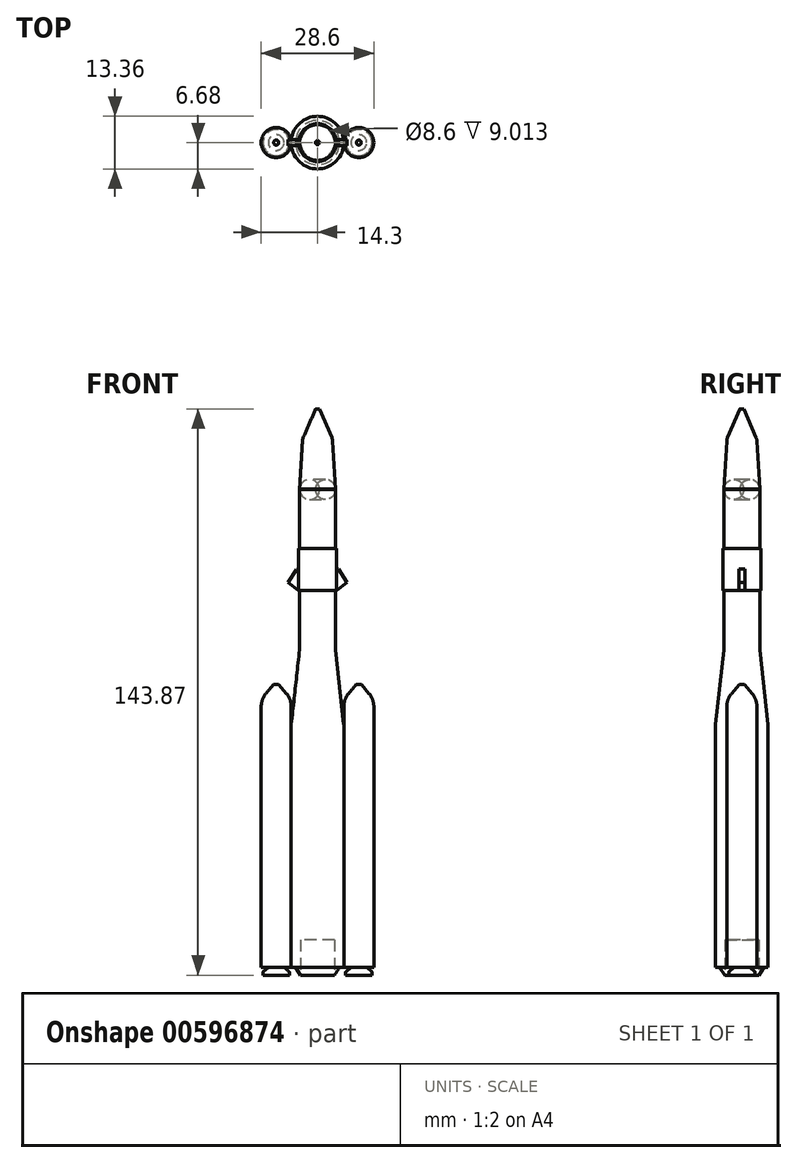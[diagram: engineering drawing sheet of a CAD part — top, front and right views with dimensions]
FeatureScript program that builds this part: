
annotation { "Feature Type Name" : "Feature", "Feature Type Description" : "" }
export const myFeature = defineFeature(function(context is Context, id is Id, definition is map)
    precondition{}
    {
        {
            var Q0;
            Q0=qCreatedBy(makeId("Front.planeOp"),FACE);
            var sketch = newSketch(context, id + "F0", { "sketchPlane" : qUnion([Q0])});
            skLineSegment(sketch, "E0", {"start": v(0, 66.06) * mm, "end": v(0, -68.1) * mm});
            skLineSegment(sketch, "E1", {"start": v(0, 66.06) * mm, "end": v(3.81, 66.06) * mm});
            skLineSegment(sketch, "E2", {"start": v(3.8, 66.06) * mm, "end": v(4.54, 53.36) * mm});
            skLineSegment(sketch, "E3", {"start": v(4.54, 53.36) * mm, "end": v(4.54, 12.72) * mm});
            skLineSegment(sketch, "E4", {"start": v(4.54, 12.72) * mm, "end": v(6.68, -6.58) * mm});
            skLineSegment(sketch, "E5", {"start": v(0, -68.1) * mm, "end": v(6.68, -68.1) * mm});
            skLineSegment(sketch, "E6", {"start": v(6.68, -6.58) * mm, "end": v(6.68, -68.1) * mm});
            skLineSegment(sketch, "E7", {"start": v(5.63, -68.1) * mm, "end": v(4.3, -70.11) * mm});
            skLineSegment(sketch, "E8", {"start": v(4.3, -70.11) * mm, "end": v(4.3, -71.56) * mm});
            skLineSegment(sketch, "E9", {"start": v(4.3, -71.56) * mm, "end": v(0, -71.56) * mm});
            skLineSegment(sketch, "E10", {"start": v(0, -71.56) * mm, "end": v(0, -68.1) * mm});
            skLineSegment(sketch, "E11", {"start": v(4.54, 33.04) * mm, "end": v(4.8, 33.04) * mm});
            skLineSegment(sketch, "E12", {"start": v(4.8, 33.04) * mm, "end": v(4.8, 27.7) * mm});
            skLineSegment(sketch, "E13", {"start": v(4.8, 27.7) * mm, "end": v(4.54, 27.7) * mm});
            skLineSegment(sketch, "E14", {"start": v(4.8, 33.04) * mm, "end": v(4.8, 38.37) * mm});
            skLineSegment(sketch, "E15", {"start": v(4.8, 38.37) * mm, "end": v(4.54, 38.37) * mm});
            skSolve(sketch);
        }
        {
            var Q0;
            Q0 = qSketchRegion(id + "F0", true);
            var Q1;
            Q1=sQuery(id+"F0.wireOp",EDGE,"E0");
            revolve(context, id + "F1", {"entities" : qUnion([Q0]), "axis" : qUnion([Q1]), "revolveType" : RevolveType.FULL});
        }
        {
            var Q0;
            Q0=qCreatedBy(makeId("Front.planeOp"),FACE);
            var sketch = newSketch(context, id + "F2", { "sketchPlane" : qUnion([Q0])});
            skLineSegment(sketch, "E16.0", {"start": v(-3.81, 66.06) * mm, "end": v(3.81, 66.06) * mm});
            skLineSegment(sketch, "E17", {"start": v(0, 66.06) * mm, "end": v(0, 73.68) * mm});
            skLineSegment(sketch, "E18", {"start": v(0.5, 73.68) * mm, "end": v(3.8, 66.06) * mm});
            skLineSegment(sketch, "E19", {"start": v(0, 73.68) * mm, "end": v(0.5, 73.68) * mm});
            skSolve(sketch);
        }
        {
            var Q0;
            Q0 = qSketchRegion(id + "F2", true);
            var Q1;
            Q1=sQuery(id+"F2.wireOp",EDGE,"E17");
            revolve(context, id + "F3", {"operationType" : NewBodyOperationType.ADD, "entities" : qUnion([Q0]), "axis" : qUnion([Q1]), "revolveType" : RevolveType.FULL});
        }
        {
            var Q0;
            Q0=qCreatedBy(makeId("Top.planeOp"),FACE);
            var sketch = newSketch(context, id + "F4", { "sketchPlane" : qUnion([Q0])});
            skCircle(sketch, "E20.0", {"center": v(0, 0) * mm, "radius": 0.5 * mm});
            skCircle(sketch, "E21.cCircle", {"center": v(0, 0) * mm, "radius": 0.23 * mm, "construction": true});
            skLineSegment(sketch, "E21.0", {"start": v(-0.1, 0.23) * mm, "end": v(0.1, 0.23) * mm});
            skLineSegment(sketch, "E21.1", {"start": v(0.1, 0.23) * mm, "end": v(0.23, 0.1) * mm});
            skLineSegment(sketch, "E21.2", {"start": v(0.23, 0.1) * mm, "end": v(0.23, -0.1) * mm});
            skLineSegment(sketch, "E21.3", {"start": v(0.23, -0.1) * mm, "end": v(0.1, -0.23) * mm});
            skLineSegment(sketch, "E21.4", {"start": v(0.1, -0.23) * mm, "end": v(-0.1, -0.23) * mm});
            skLineSegment(sketch, "E21.5", {"start": v(-0.1, -0.23) * mm, "end": v(-0.23, -0.1) * mm});
            skLineSegment(sketch, "E21.6", {"start": v(-0.23, -0.1) * mm, "end": v(-0.23, 0.1) * mm});
            skLineSegment(sketch, "E21.7", {"start": v(-0.23, 0.1) * mm, "end": v(-0.1, 0.23) * mm});
            skPoint(sketch, "E21.0.midPoint", {"position": v(0, 0.23) * mm});
            skSolve(sketch);
        }
        {
            var Q0;
            Q0 = qSketchRegion(id + "F4", true);
            extrude(context, id + "F5", {"entities" : qUnion([Q0]), "operationType" : NewBodyOperationType.ADD, "depth" : 73.76 * mm, "offsetDistance" : 25.4 * mm});
        }
        {
            var Q0;
            Q0=makeQuery(id+"F3.boolean.opBoolean","MERGE",EDGE,{"derivedFrom":[makeQuery(id+"F1.opRevolve","SWEPT_EDGE",EDGE,{"disambiguationData":[OSD([sQuery(id+"F0.wireOp",EDGE,"E1"),sQuery(id+"F0.wireOp",EDGE,"E2")])]}),makeQuery(id+"F3.opRevolve","SWEPT_EDGE",EDGE,{"disambiguationData":[OSD([sQuery(id+"F2.wireOp",EDGE,"E16.0"),sQuery(id+"F2.wireOp",EDGE,"E18")])]})]});
            var Q1;
            Q1=makeQuery(id+"F1.opRevolve","SWEPT_EDGE",EDGE,{"disambiguationData":[OSD([sQuery(id+"F0.wireOp",EDGE,"E2"),sQuery(id+"F0.wireOp",EDGE,"E3")])]});
            var Q2;
            Q2=makeQuery(id+"F1.opRevolve","SWEPT_EDGE",EDGE,{"disambiguationData":[OSD([sQuery(id+"F0.wireOp",EDGE,"E3"),sQuery(id+"F0.wireOp",EDGE,"E4")])]});
            var Q3;
            Q3=makeQuery(id+"F1.opRevolve","SWEPT_EDGE",EDGE,{"disambiguationData":[OSD([sQuery(id+"F0.wireOp",EDGE,"E4"),sQuery(id+"F0.wireOp",EDGE,"E6")])]});
            fillet(context, id + "F6", {"entities" : qUnion([Q0, Q1, Q2, Q3]), "radius" : 2.54 * mm, "tangentPropagation" : true, "allowEdgeOverflow" : false});
        }
        {
            var Q0;
            Q0=qCreatedBy(makeId("Top.planeOp"),FACE);
            var sketch = newSketch(context, id + "F7", { "sketchPlane" : qUnion([Q0])});
            skCircle(sketch, "E22.0.0", {"center": v(0, 0) * mm, "radius": 6.68 * mm});
            skLineSegment(sketch, "E23", {"start": v(6.68, 0) * mm, "end": v(10.5, 0) * mm});
            skLineSegment(sketch, "E24", {"start": v(-6.68, 0) * mm, "end": v(-10.5, 0) * mm});
            skPoint(sketch, "E25.0.midPoint", {"position": v(-6.68, 0) * mm});
            skPoint(sketch, "E26.0.midPoint", {"position": v(6.68, 0) * mm});
            skCircle(sketch, "E27", {"center": v(10.5, 0) * mm, "radius": 3.81 * mm});
            skCircle(sketch, "E28", {"center": v(-10.5, 0) * mm, "radius": 3.81 * mm});
            skSolve(sketch);
        }
        {
            var Q0;
            Q0=makeQuery(id+"F7.imprint","IMPRINT",FACE,{"disambiguationData":[TD([[makeQuery(id+"F7.imprint","IMPRINT",EDGE,{"derivedFrom":sQuery(id+"F7.wireOp",EDGE,"E28")}),1.0]])]});
            var Q1;
            Q1=makeQuery(id+"F7.imprint","IMPRINT",FACE,{"disambiguationData":[TD([[makeQuery(id+"F7.imprint","IMPRINT",EDGE,{"derivedFrom":sQuery(id+"F7.wireOp",EDGE,"E27")}),1.0]])]});
            extrude(context, id + "F8", {"entities" : qUnion([Q0, Q1]), "oppositeDirection" : true, "depth" : 68.07 * mm, "offsetDistance" : 25.4 * mm});
        }
        {
            var Q0;
            Q0=qCreatedBy(makeId("Front.planeOp"),FACE);
            var sketch = newSketch(context, id + "F9", { "sketchPlane" : qUnion([Q0])});
            skLineSegment(sketch, "E29.0", {"start": v(-14.3, 0) * mm, "end": v(-6.68, 0) * mm});
            skLineSegment(sketch, "E30.0", {"start": v(6.68, 0) * mm, "end": v(14.3, 0) * mm});
            skLineSegment(sketch, "E31", {"start": v(10.5, 0) * mm, "end": v(10.5, 3.81) * mm});
            skLineSegment(sketch, "E32", {"start": v(10.5, 3.81) * mm, "end": v(11.12, 3.81) * mm});
            skLineSegment(sketch, "E33", {"start": v(11.12, 3.81) * mm, "end": v(14.3, 0) * mm});
            skSolve(sketch);
        }
        {
            var Q0;
            Q0=qCreatedBy(makeId("Front.planeOp"),FACE);
            var sketch = newSketch(context, id + "F10", { "sketchPlane" : qUnion([Q0])});
            skLineSegment(sketch, "E34", {"start": v(-6.68, 0) * mm, "end": v(-6.68, -68.07) * mm});
            skLineSegment(sketch, "E35", {"start": v(-14.3, -68.07) * mm, "end": v(-14.3, 0) * mm});
            skLineSegment(sketch, "E36.0", {"start": v(-14.3, 0) * mm, "end": v(-6.68, 0) * mm});
            skLineSegment(sketch, "E37", {"start": v(-10.5, 0) * mm, "end": v(-10.5, 3.81) * mm});
            skLineSegment(sketch, "E38", {"start": v(-10.5, 3.81) * mm, "end": v(-11.14, 3.81) * mm});
            skLineSegment(sketch, "E39", {"start": v(-11.14, 3.81) * mm, "end": v(-14.3, 0) * mm});
            skSolve(sketch);
        }
        {
            var Q0;
            Q0 = qSketchRegion(id + "F10", true);
            var Q1;
            Q1=sQuery(id+"F10.wireOp",EDGE,"E37");
            revolve(context, id + "F11", {"operationType" : NewBodyOperationType.ADD, "entities" : qUnion([Q0]), "axis" : qUnion([Q1]), "revolveType" : RevolveType.FULL});
        }
        {
            var Q0;
            Q0=makeQuery(id+"F11.boolean.opBoolean","MERGE",EDGE,{"derivedFrom":[makeQuery(id+"F8.opExtrude","CAP_EDGE",EDGE,{"disambiguationData":[OSD([sQuery(id+"F7.wireOp",EDGE,"E28")])],"isStart":true}),makeQuery(id+"F11.opRevolve","SWEPT_EDGE",EDGE,{"disambiguationData":[OSD([sQuery(id+"F10.wireOp",EDGE,"E36.0"),sQuery(id+"F10.wireOp",EDGE,"E39")])]})]});
            fillet(context, id + "F12", {"entities" : qUnion([Q0]), "radius" : 5.08 * mm, "tangentPropagation" : true, "allowEdgeOverflow" : false});
        }
        {
            var Q0;
            Q0 = qSketchRegion(id + "F9", true);
            var Q1;
            Q1=sQuery(id+"F9.wireOp",EDGE,"E31");
            revolve(context, id + "F13", {"operationType" : NewBodyOperationType.ADD, "entities" : qUnion([Q0]), "axis" : qUnion([Q1]), "revolveType" : RevolveType.FULL});
        }
        {
            var Q0;
            Q0=makeQuery(id+"F13.boolean.opBoolean","MERGE",EDGE,{"derivedFrom":[makeQuery(id+"F8.opExtrude","CAP_EDGE",EDGE,{"disambiguationData":[OSD([sQuery(id+"F7.wireOp",EDGE,"E27")])],"isStart":true}),makeQuery(id+"F13.opRevolve","SWEPT_EDGE",EDGE,{"disambiguationData":[OSD([sQuery(id+"F9.wireOp",EDGE,"E30.0"),sQuery(id+"F9.wireOp",EDGE,"E33")])]})]});
            fillet(context, id + "F14", {"entities" : qUnion([Q0]), "radius" : 5.08 * mm, "tangentPropagation" : true, "allowEdgeOverflow" : false});
        }
        {
            var Q0;
            Q0=makeQuery(id+"F1.opRevolve","SWEPT_FACE",FACE,{"disambiguationData":[OSD([sQuery(id+"F0.wireOp",EDGE,"E9")])]});
            extrude(context, id + "F15", {"entities" : qUnion([Q0]), "operationType" : NewBodyOperationType.REMOVE, "oppositeDirection" : true, "depth" : 10.46 * mm, "offsetDistance" : 25.4 * mm});
        }
        {
            var Q0;
            Q0=qCreatedBy(makeId("Front.planeOp"),FACE);
            var sketch = newSketch(context, id + "F16", { "sketchPlane" : qUnion([Q0])});
            skLineSegment(sketch, "E40", {"start": v(14.3, -1.84) * mm, "end": v(14.3, -68.07) * mm});
            skLineSegment(sketch, "E41", {"start": v(6.68, -68.07) * mm, "end": v(6.68, -1.84) * mm});
            skLineSegment(sketch, "E42.0", {"start": v(6.68, -68.07) * mm, "end": v(14.3, -68.07) * mm});
            skLineSegment(sketch, "E43", {"start": v(5.63, -68.1) * mm, "end": v(4.3, -70.11) * mm});
            skLineSegment(sketch, "E44", {"start": v(-4.3, -70.11) * mm, "end": v(-5.63, -68.1) * mm});
            skLineSegment(sketch, "E45", {"start": v(10.5, -68.07) * mm, "end": v(10.5, -70.11) * mm});
            skLineSegment(sketch, "E46", {"start": v(10.5, -70.11) * mm, "end": v(13.83, -70.11) * mm});
            skLineSegment(sketch, "E47", {"start": v(13.83, -70.11) * mm, "end": v(13.83, -69.25) * mm});
            skLineSegment(sketch, "E48", {"start": v(13.83, -69.25) * mm, "end": v(12.5, -68.07) * mm});
            skSolve(sketch);
        }
        {
            var Q0;
            Q0 = qSketchRegion(id + "F16", true);
            var Q1;
            Q1=sQuery(id+"F16.wireOp",EDGE,"E45");
            revolve(context, id + "F17", {"operationType" : NewBodyOperationType.ADD, "entities" : qUnion([Q0]), "axis" : qUnion([Q1]), "revolveType" : RevolveType.FULL});
        }
        {
            var Q0;
            Q0=makeQuery(id+"F17.opRevolve","SWEPT_EDGE",EDGE,{"disambiguationData":[OSD([sQuery(id+"F16.wireOp",EDGE,"E47"),sQuery(id+"F16.wireOp",EDGE,"E48")])]});
            fillet(context, id + "F18", {"entities" : qUnion([Q0]), "radius" : 0.1 * mm, "tangentPropagation" : true, "allowEdgeOverflow" : false});
        }
        {
            var Q0;
            Q0=qCreatedBy(makeId("Front.planeOp"),FACE);
            var sketch = newSketch(context, id + "F19", { "sketchPlane" : qUnion([Q0])});
            skLineSegment(sketch, "E49", {"start": v(5.63, -68.1) * mm, "end": v(4.3, -70.11) * mm});
            skLineSegment(sketch, "E50", {"start": v(-4.3, -70.11) * mm, "end": v(-5.63, -68.1) * mm});
            skLineSegment(sketch, "E51.0", {"start": v(-14.3, -68.07) * mm, "end": v(-6.68, -68.07) * mm});
            skLineSegment(sketch, "E52", {"start": v(-10.5, -68.07) * mm, "end": v(-10.5, -70.11) * mm});
            skLineSegment(sketch, "E53", {"start": v(-10.5, -70.11) * mm, "end": v(-13.82, -70.11) * mm});
            skLineSegment(sketch, "E54", {"start": v(-13.82, -70.11) * mm, "end": v(-13.82, -69.26) * mm});
            skLineSegment(sketch, "E55", {"start": v(-13.82, -69.26) * mm, "end": v(-12.49, -68.07) * mm});
            skSolve(sketch);
        }
        {
            var Q0;
            Q0 = qSketchRegion(id + "F19", true);
            var Q1;
            Q1=sQuery(id+"F19.wireOp",EDGE,"E52");
            revolve(context, id + "F20", {"operationType" : NewBodyOperationType.ADD, "entities" : qUnion([Q0]), "axis" : qUnion([Q1]), "revolveType" : RevolveType.FULL});
        }
        {
            var Q0;
            Q0=makeQuery(id+"F20.opRevolve","SWEPT_EDGE",EDGE,{"disambiguationData":[OSD([sQuery(id+"F19.wireOp",EDGE,"E54"),sQuery(id+"F19.wireOp",EDGE,"E55")])]});
            fillet(context, id + "F21", {"entities" : qUnion([Q0]), "radius" : 0.1 * mm, "tangentPropagation" : true, "allowEdgeOverflow" : false});
        }
        {
            var Q0;
            Q0=qCreatedBy(makeId("Front.planeOp"),FACE);
            var sketch = newSketch(context, id + "F22", { "sketchPlane" : qUnion([Q0])});
            skLineSegment(sketch, "E56", {"start": v(4.8, 38.45) * mm, "end": v(4.8, 27.7) * mm});
            skLineSegment(sketch, "E57", {"start": v(-4.8, 27.7) * mm, "end": v(-4.8, 38.37) * mm});
            skLineSegment(sketch, "E58", {"start": v(4.8, 33.08) * mm, "end": v(5.3, 33.08) * mm});
            skLineSegment(sketch, "E59", {"start": v(5.3, 33.08) * mm, "end": v(7.5, 29.67) * mm});
            skLineSegment(sketch, "E60", {"start": v(7.5, 29.67) * mm, "end": v(4.8, 27.7) * mm});
            skLineSegment(sketch, "E61", {"start": v(-4.8, 33.03) * mm, "end": v(-5.3, 33.03) * mm});
            skPoint(sketch, "E61.endSnap0", {"position": v(-4.8, 33.03) * mm});
            skLineSegment(sketch, "E62", {"start": v(-5.3, 33.03) * mm, "end": v(-7.5, 29.66) * mm});
            skLineSegment(sketch, "E63", {"start": v(-7.5, 29.66) * mm, "end": v(-4.8, 27.7) * mm});
            skSolve(sketch);
        }
        {
            var Q0;
            Q0 = qSketchRegion(id + "F22", true);
            extrude(context, id + "F23", {"entities" : qUnion([Q0]), "operationType" : NewBodyOperationType.ADD, "endBound" : BoundingType.SYMMETRIC, "depth" : 1.52 * mm, "offsetDistance" : 25.4 * mm});
        }
    });
